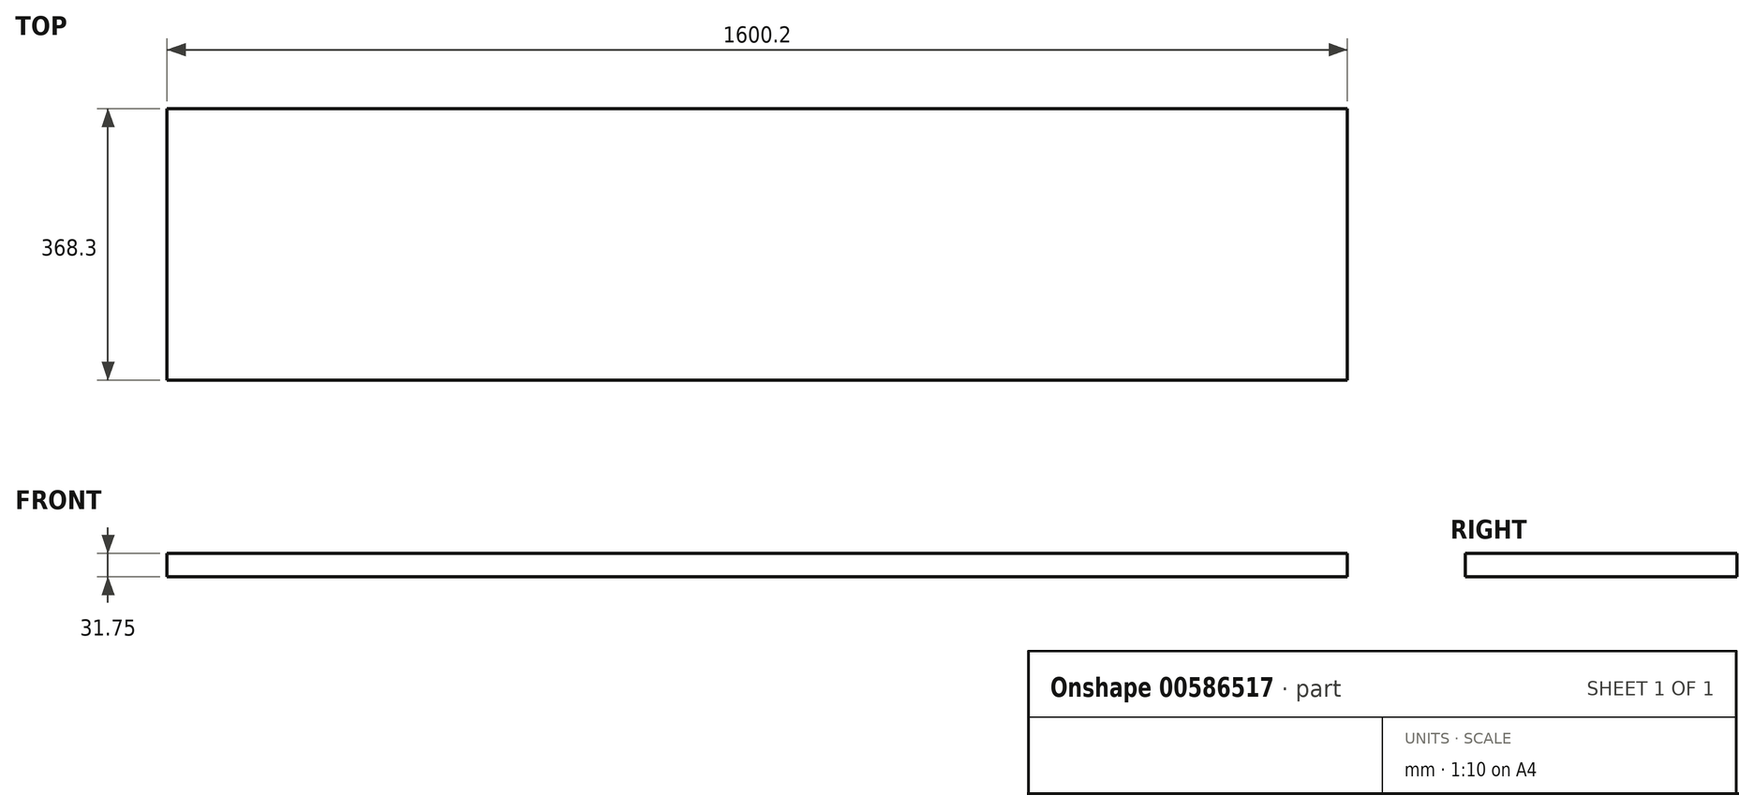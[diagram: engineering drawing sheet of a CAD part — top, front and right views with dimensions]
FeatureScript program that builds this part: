
annotation { "Feature Type Name" : "Feature", "Feature Type Description" : "" }
export const myFeature = defineFeature(function(context is Context, id is Id, definition is map)
    precondition{}
    {
        {
            var Q0;
            Q0=qCreatedBy(makeId("Front.planeOp"),FACE);
            var sketch = newSketch(context, id + "F0", { "sketchPlane" : qUnion([Q0])});
            skLineSegment(sketch, "E0.bottom", {"start": v(0, 0) * mm, "end": v(1600.2, 0) * mm});
            skLineSegment(sketch, "E0.top", {"start": v(0, 31.75) * mm, "end": v(1600.2, 31.75) * mm});
            skLineSegment(sketch, "E0.left", {"start": v(0, 0) * mm, "end": v(0, 31.75) * mm});
            skLineSegment(sketch, "E0.right", {"start": v(1600.2, 0) * mm, "end": v(1600.2, 31.75) * mm});
            skSolve(sketch);
        }
        {
            var Q0;
            Q0 = qSketchRegion(id + "F0", true);
            extrude(context, id + "F1", {"entities" : qUnion([Q0]), "depth" : 368.3 * mm, "offsetDistance" : 25.4 * mm});
        }
    });
